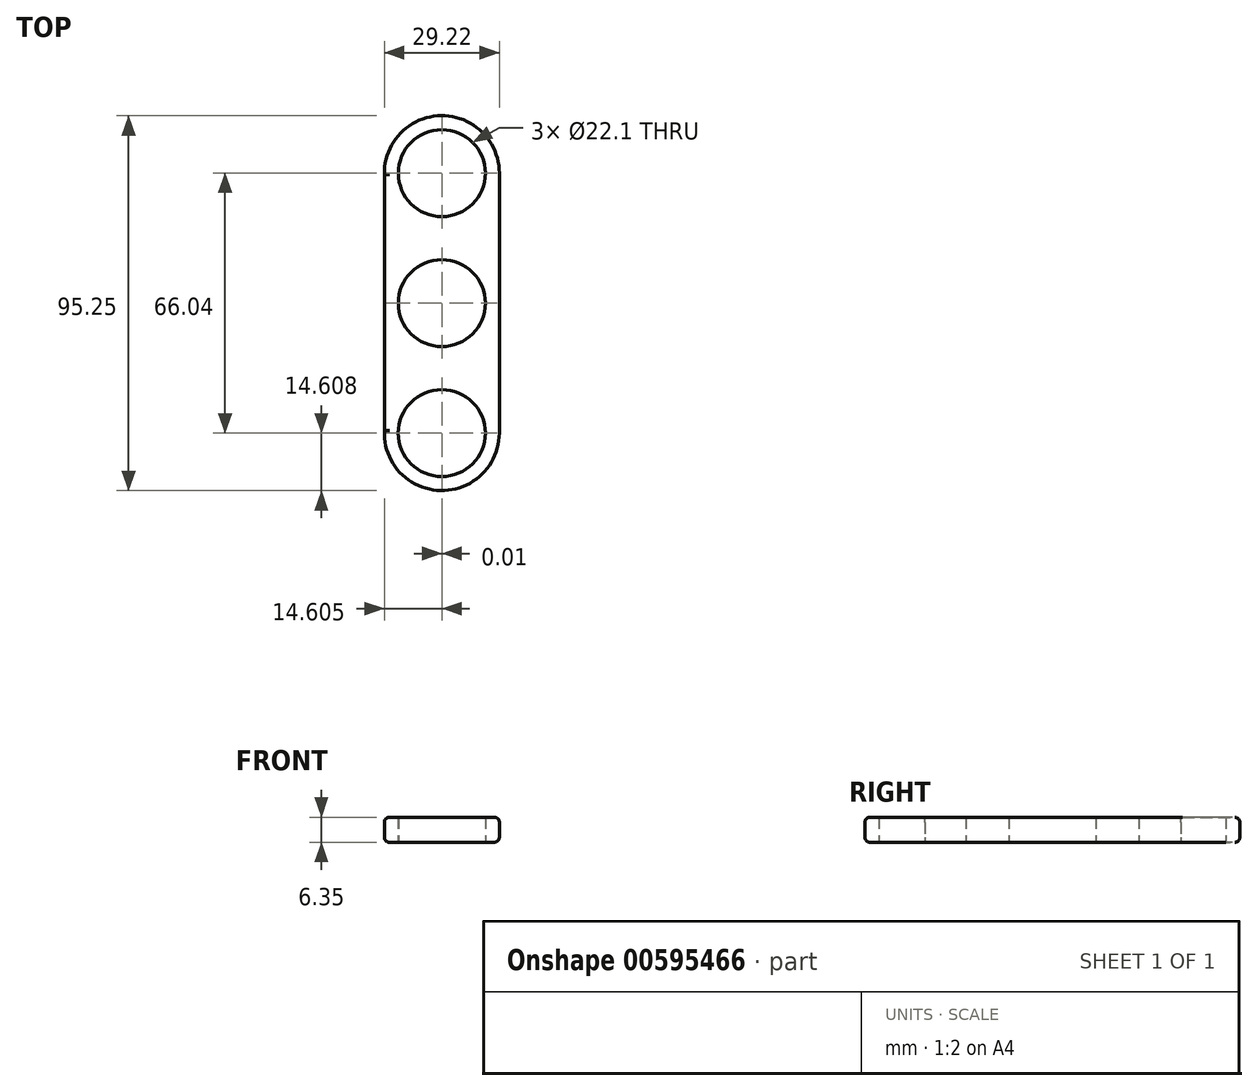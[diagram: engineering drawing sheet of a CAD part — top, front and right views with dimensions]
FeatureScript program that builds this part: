
annotation { "Feature Type Name" : "Feature", "Feature Type Description" : "" }
export const myFeature = defineFeature(function(context is Context, id is Id, definition is map)
    precondition{}
    {
        {
            var Q0;
            Q0=qCreatedBy(makeId("Top.planeOp"),FACE);
            var sketch = newSketch(context, id + "F0", { "sketchPlane" : qUnion([Q0])});
            skCircle(sketch, "E0", {"center": v(0, 0) * mm, "radius": 11.05 * mm});
            skCircle(sketch, "E1", {"center": v(0, 33.02) * mm, "radius": 11.05 * mm});
            skCircle(sketch, "E2", {"center": v(0, -33.02) * mm, "radius": 11.05 * mm});
            skCircle(sketch, "E3", {"center": v(0, 33.02) * mm, "radius": 14.6 * mm});
            skCircle(sketch, "E4", {"center": v(0, -33.02) * mm, "radius": 14.6 * mm});
            skLineSegment(sketch, "E5", {"start": v(-14.6, 33.34) * mm, "end": v(-14.6, -33.66) * mm});
            skLineSegment(sketch, "E6", {"start": v(14.61, 33.02) * mm, "end": v(14.6, -33.02) * mm});
            skSolve(sketch);
        }
        {
            var Q0;
            Q0 = qSketchRegion(id + "F0", true);
            extrude(context, id + "F1", {"entities" : qUnion([Q0]), "depth" : 6.35 * mm, "offsetDistance" : 25.4 * mm});
        }
        {
            var Q0;
            Q0=makeQuery(id+"F1.opExtrude","CAP_EDGE",EDGE,{"disambiguationData":[OSD([sQuery(id+"F0.wireOp",EDGE,"E6")])],"isStart":true});
            var Q1;
            Q1=makeQuery(id+"F1.opExtrude","CAP_EDGE",EDGE,{"disambiguationData":[OSD([sQuery(id+"F0.wireOp",EDGE,"E6")])],"isStart":false});
            var Q2;
            Q2=makeQuery(id+"F1.opExtrude","CAP_EDGE",EDGE,{"disambiguationData":[OSD([sQuery(id+"F0.wireOp",EDGE,"E4")])],"isStart":true});
            var Q3;
            Q3=makeQuery(id+"F1.opExtrude","CAP_EDGE",EDGE,{"disambiguationData":[OSD([sQuery(id+"F0.wireOp",EDGE,"E3")])],"isStart":true});
            var Q4;
            Q4=makeQuery(id+"F1.opExtrude","CAP_EDGE",EDGE,{"disambiguationData":[OSD([sQuery(id+"F0.wireOp",EDGE,"E3")])],"isStart":false});
            var Q5;
            Q5=makeQuery(id+"F1.opExtrude","CAP_EDGE",EDGE,{"disambiguationData":[OSD([sQuery(id+"F0.wireOp",EDGE,"E5")])],"isStart":false});
            var Q6;
            Q6=makeQuery(id+"F1.opExtrude","CAP_EDGE",EDGE,{"disambiguationData":[OSD([sQuery(id+"F0.wireOp",EDGE,"E4")])],"isStart":false});
            var Q7;
            Q7=makeQuery(id+"F1.opExtrude","CAP_EDGE",EDGE,{"disambiguationData":[OSD([sQuery(id+"F0.wireOp",EDGE,"E5")])],"isStart":true});
            fillet(context, id + "F2", {"entities" : qUnion([Q0, Q1, Q2, Q3, Q4, Q5, Q6, Q7]), "radius" : 1.27 * mm, "tangentPropagation" : true, "allowEdgeOverflow" : false});
        }
    });
